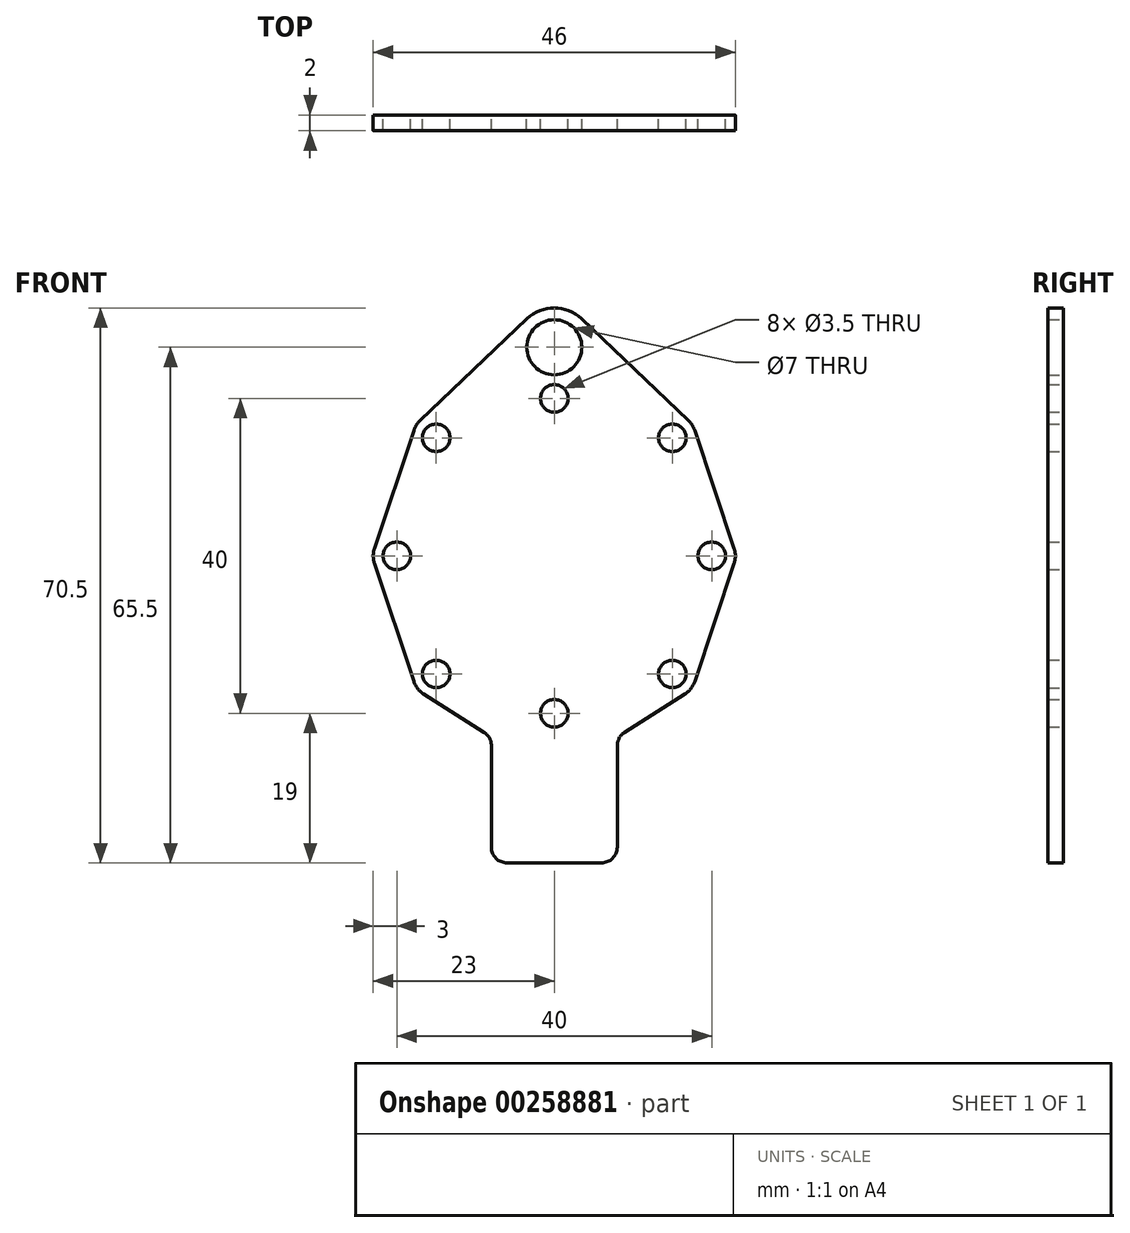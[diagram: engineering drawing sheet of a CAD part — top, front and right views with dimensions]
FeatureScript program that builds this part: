
annotation { "Feature Type Name" : "Feature", "Feature Type Description" : "" }
export const myFeature = defineFeature(function(context is Context, id is Id, definition is map)
    precondition{}
    {
        {
            var Q0;
            Q0=qCreatedBy(makeId("Front.planeOp"),FACE);
            var sketch = newSketch(context, id + "F0", { "sketchPlane" : qUnion([Q0])});
            skPoint(sketch, "E0", {"position": v(0, 0) * mm});
            skPoint(sketch, "E1", {"position": v(-15, 15) * mm});
            skPoint(sketch, "E2", {"position": v(15, 15) * mm});
            skPoint(sketch, "E3", {"position": v(15, -15) * mm});
            skPoint(sketch, "E4", {"position": v(-15, -15) * mm});
            skPoint(sketch, "E5", {"position": v(0, -20) * mm});
            skPoint(sketch, "E6.1.0", {"position": v(20, 0) * mm});
            skPoint(sketch, "E6.2.0", {"position": v(0, 20) * mm});
            skPoint(sketch, "E6.3.0", {"position": v(-20, 0) * mm});
            skCircle(sketch, "E7", {"center": v(0, -20) * mm, "radius": 1.75 * mm});
            skCircle(sketch, "E8", {"center": v(15, -15) * mm, "radius": 1.75 * mm});
            skCircle(sketch, "E9", {"center": v(20, 0) * mm, "radius": 1.75 * mm});
            skCircle(sketch, "E10", {"center": v(15, 15) * mm, "radius": 1.75 * mm});
            skCircle(sketch, "E11", {"center": v(0, 20) * mm, "radius": 1.75 * mm});
            skCircle(sketch, "E12", {"center": v(-15, 15) * mm, "radius": 1.75 * mm});
            skCircle(sketch, "E13", {"center": v(-20, 0) * mm, "radius": 1.75 * mm});
            skCircle(sketch, "E14", {"center": v(-15, -15) * mm, "radius": 1.75 * mm});
            skArc(sketch, "E15", {"start": v(16.6, -17.53) * mm, "mid": v(17.36, -16.85) * mm, "end": v(17.85, -15.95) * mm});
            skArc(sketch, "E16", {"start": v(22.85, -0.95) * mm, "mid": v(23, 0) * mm, "end": v(22.85, 0.95) * mm});
            skArc(sketch, "E17", {"start": v(17.85, 15.95) * mm, "mid": v(17.53, 16.6) * mm, "end": v(17.07, 17.17) * mm});
            skArc(sketch, "E18", {"start": v(-17.07, 17.17) * mm, "mid": v(-17.53, 16.6) * mm, "end": v(-17.85, 15.95) * mm});
            skArc(sketch, "E19", {"start": v(-22.85, 0.95) * mm, "mid": v(-23, 0) * mm, "end": v(-22.85, -0.95) * mm});
            skArc(sketch, "E20", {"start": v(-17.85, -15.95) * mm, "mid": v(-17.36, -16.85) * mm, "end": v(-16.6, -17.53) * mm});
            skLineSegment(sketch, "E21", {"start": v(0, 23) * mm, "end": v(0, 26.5) * mm, "construction": true});
            skCircle(sketch, "E22", {"center": v(0, 26.5) * mm, "radius": 3.5 * mm});
            skArc(sketch, "E23", {"start": v(3.44, 30.12) * mm, "mid": v(0, 31.5) * mm, "end": v(-3.44, 30.12) * mm});
            skLineSegment(sketch, "E24", {"start": v(0, -23) * mm, "end": v(0, -39) * mm, "construction": true});
            skLineSegment(sketch, "E25", {"start": v(0, -23) * mm, "end": v(8, -23) * mm, "construction": true});
            skLineSegment(sketch, "E26", {"start": v(8, -24.1) * mm, "end": v(8, -37) * mm});
            skLineSegment(sketch, "E27", {"start": v(6, -39) * mm, "end": v(-6, -39) * mm});
            skLineSegment(sketch, "E28", {"start": v(-8, -37) * mm, "end": v(-8, -24.1) * mm});
            skLineSegment(sketch, "E29", {"start": v(-3.44, 30.12) * mm, "end": v(-17.07, 17.17) * mm});
            skLineSegment(sketch, "E30", {"start": v(-17.85, 15.95) * mm, "end": v(-22.85, 0.95) * mm});
            skLineSegment(sketch, "E31", {"start": v(-22.85, -0.95) * mm, "end": v(-17.85, -15.95) * mm});
            skLineSegment(sketch, "E32", {"start": v(17.85, -15.95) * mm, "end": v(22.85, -0.95) * mm});
            skLineSegment(sketch, "E33", {"start": v(22.85, 0.95) * mm, "end": v(17.85, 15.95) * mm});
            skLineSegment(sketch, "E34", {"start": v(17.07, 17.17) * mm, "end": v(3.44, 30.12) * mm});
            skLineSegment(sketch, "E35", {"start": v(-8.93, -22.41) * mm, "end": v(-16.6, -17.53) * mm});
            skLineSegment(sketch, "E36", {"start": v(8.93, -22.41) * mm, "end": v(16.6, -17.53) * mm});
            skPoint(sketch, "E37.visualSharp", {"position": v(8, -39) * mm});
            skArc(sketch, "E37.filletArc", {"start": v(6, -39) * mm, "mid": v(7.41, -38.41) * mm, "end": v(8, -37) * mm});
            skPoint(sketch, "E38.visualSharp", {"position": v(-8, -39) * mm});
            skArc(sketch, "E38.filletArc", {"start": v(-8, -37) * mm, "mid": v(-7.41, -38.41) * mm, "end": v(-6, -39) * mm});
            skPoint(sketch, "E39.visualSharp", {"position": v(8, -23) * mm});
            skArc(sketch, "E39.filletArc", {"start": v(8.93, -22.41) * mm, "mid": v(8.25, -23.14) * mm, "end": v(8, -24.1) * mm});
            skPoint(sketch, "E40.visualSharp", {"position": v(-8, -23) * mm});
            skArc(sketch, "E40.filletArc", {"start": v(-8, -24.1) * mm, "mid": v(-8.25, -23.14) * mm, "end": v(-8.93, -22.41) * mm});
            skSolve(sketch);
        }
        {
            var Q0;
            Q0=makeQuery(id+"F0.imprint","IMPRINT",FACE,{"disambiguationData":[TD([[makeQuery(id+"F0.imprint","IMPRINT",EDGE,{"derivedFrom":sQuery(id+"F0.wireOp",EDGE,"E7")}),-1.0]])]});
            extrude(context, id + "F1", {"entities" : qUnion([Q0]), "depth" : 2 * mm});
        }
    });
